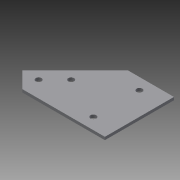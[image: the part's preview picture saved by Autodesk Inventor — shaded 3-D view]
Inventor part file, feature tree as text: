
AUTODESK INVENTOR PART (.ipt)
format: ipt  version: 2013 (Build 170138000, 138)  size: 94,208 bytes
history: native  units: in
note: dims shown in document units (in); Inventor stores cm internally (conversion verified against a paired STEP export)
features: extrude x1, sketch x1
ambient origin geometry x8: Origin, YZ Plane, XZ Plane, XY Plane, X Axis, Y Axis, Z Axis, Center Point
bodies: Solid1 (feature_tree)
feature tree (2):
  extrude  "Extrusion1"  TaperAngle=180.0deg  [1 undecoded]
  sketch  "Sketch1"  dims[d0=2.0in d1=180.0deg d2=0.5in d3=90.0deg d4=0.25in d5=2.0in d6=0.25in d7=3.0in d8=90.0deg d9=45.0deg d10=1.0in d11=135.0deg d12=0.5in d13=135.0deg d14=1.0in d15=180.0deg d16=0.25in d17=0.25in d18=0.125in d19=0.0in]
note: 1 required parameter value undecoded (feature->parameter linkage not recoverable at this tier; creation-order binding heuristic only, values carry confidence <= 0.55)
